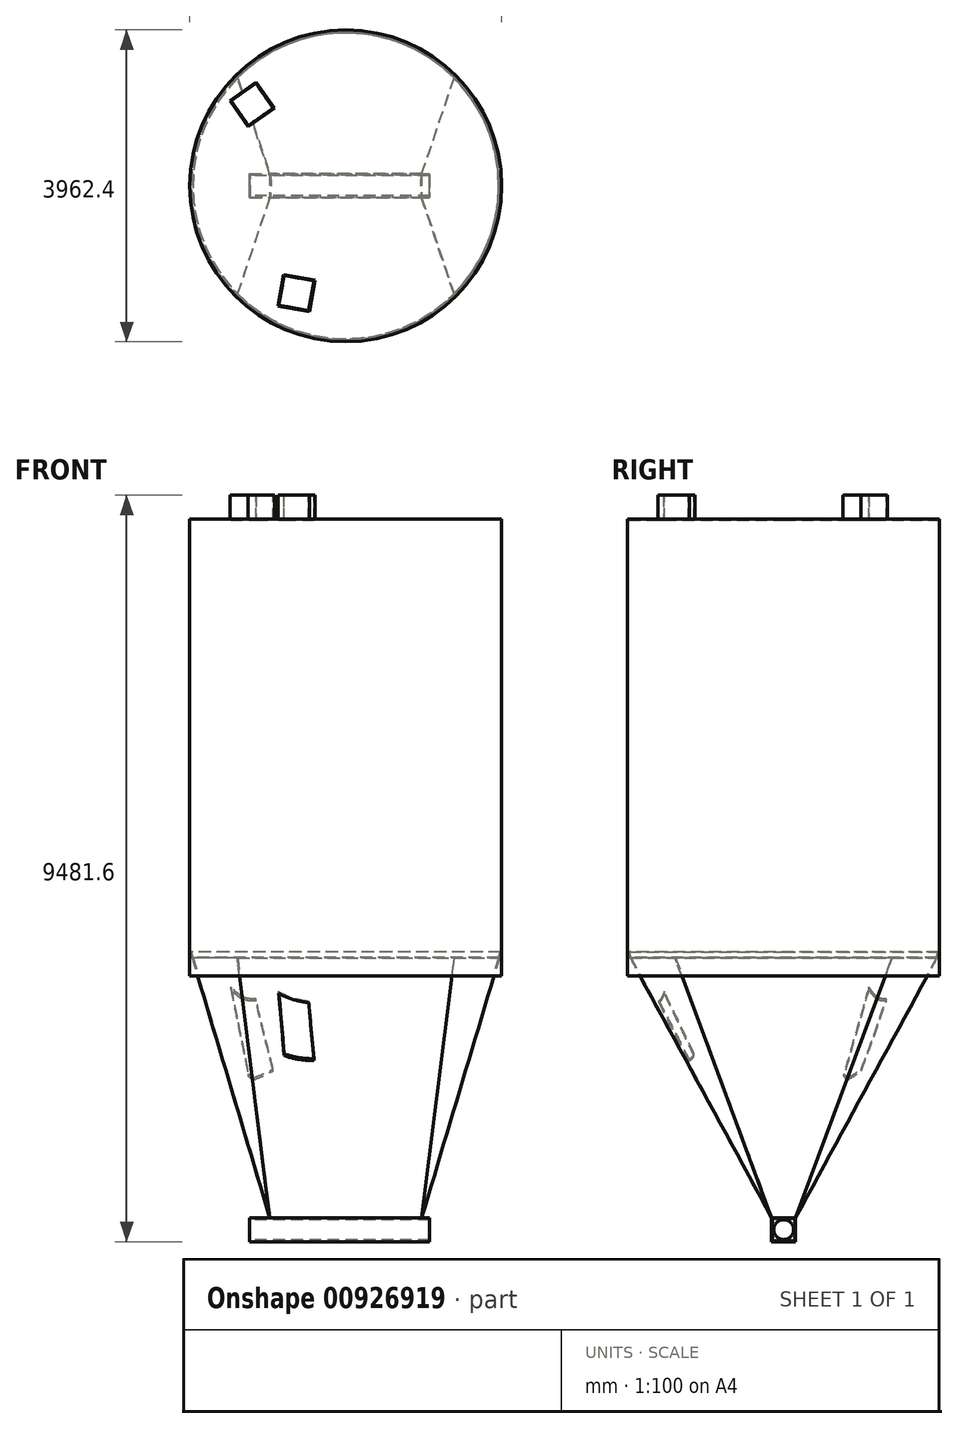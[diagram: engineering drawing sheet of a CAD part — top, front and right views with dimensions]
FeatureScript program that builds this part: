
annotation { "Feature Type Name" : "Feature", "Feature Type Description" : "" }
export const myFeature = defineFeature(function(context is Context, id is Id, definition is map)
    precondition{}
    {
        {
            var Q0;
            Q0=qCreatedBy(makeId("Front.planeOp"),FACE);
            var sketch = newSketch(context, id + "F0", { "sketchPlane" : qUnion([Q0])});
            skLineSegment(sketch, "E0", {"start": v(-1971.2, 73.6) * mm, "end": v(-1961.54, 76.2) * mm});
            skLineSegment(sketch, "E1", {"start": v(-1961.54, 76.2) * mm, "end": v(-1941.82, 2.59) * mm});
            skLineSegment(sketch, "E2", {"start": v(-1941.82, 2.59) * mm, "end": v(-1951.48, 0) * mm});
            skLineSegment(sketch, "E3", {"start": v(-1951.48, 0) * mm, "end": v(-1971.2, 73.6) * mm});
            skLineSegment(sketch, "E4", {"start": v(0, 190.18) * mm, "end": v(0, -283.34) * mm, "construction": true});
            skLineSegment(sketch, "E5.bottom", {"start": v(-1981.2, 5560) * mm, "end": v(-1971.2, 5560) * mm});
            skLineSegment(sketch, "E5.top", {"start": v(-1981.2, -231.2) * mm, "end": v(-1971.2, -231.2) * mm});
            skLineSegment(sketch, "E5.left", {"start": v(-1981.2, 5560) * mm, "end": v(-1981.2, -231.2) * mm});
            skLineSegment(sketch, "E5.right", {"start": v(-1971.2, 5560) * mm, "end": v(-1971.2, -231.2) * mm});
            skSolve(sketch);
        }
        {
            var Q0;
            Q0 = qSketchRegion(id + "F0", true);
            var Q1;
            Q1=sQuery(id+"F0.wireOp",EDGE,"E4");
            revolve(context, id + "F1", {"surfaceOperationType" : NewSurfaceOperationType.NEW, "entities" : qUnion([Q0]), "axis" : qUnion([Q1]), "revolveType" : RevolveType.FULL});
        }
        {
            var Q0;
            Q0=makeQuery(id+"F1.opRevolve","SWEPT_FACE",FACE,{"disambiguationData":[OSD([sQuery(id+"F0.wireOp",EDGE,"E5.bottom")])]});
            var sketch = newSketch(context, id + "F2", { "sketchPlane" : qUnion([Q0])});
            skCircle(sketch, "E6.0", {"center": v(0, 0) * mm, "radius": 1981.2 * mm});
            skSolve(sketch);
        }
        {
            var Q0;
            Q0 = qSketchRegion(id + "F2", true);
            extrude(context, id + "F3", {"entities" : qUnion([Q0]), "operationType" : NewBodyOperationType.ADD, "depth" : 10 * mm, "offsetDistance" : 25.4 * mm});
        }
        {
            var Q0;
            Q0=qCreatedBy(makeId("Top.planeOp"),FACE);
            cPlane(context, id + "F4", {"entities" : qUnion([Q0]), "cplaneType" : CPlaneType.OFFSET, "offset" : 3302 * mm, "oppositeDirection" : true, "width" : 152.4 * mm, "height" : 152.4 * mm});
        }
        {
            var Q0;
            Q0=qCreatedBy(id+"F4.planeOp",FACE);
            var sketch = newSketch(context, id + "F5", { "sketchPlane" : qUnion([Q0])});
            skLineSegment(sketch, "E7.bottom", {"start": v(965.2, 152.4) * mm, "end": v(-965.2, 152.4) * mm});
            skLineSegment(sketch, "E7.top", {"start": v(965.2, -152.4) * mm, "end": v(-965.2, -152.4) * mm});
            skLineSegment(sketch, "E7.left", {"start": v(965.2, 152.4) * mm, "end": v(965.2, -152.4) * mm});
            skLineSegment(sketch, "E7.right", {"start": v(-965.2, 152.4) * mm, "end": v(-965.2, -152.4) * mm});
            skPoint(sketch, "E7.middle", {"position": v(0, 0) * mm});
            skSolve(sketch);
        }
        {
            var Q0;
            Q0=qCreatedBy(makeId("Top.planeOp"),FACE);
            var sketch = newSketch(context, id + "F6", { "sketchPlane" : qUnion([Q0])});
            skCircle(sketch, "E8.0", {"center": v(0, 0) * mm, "radius": 1951.48 * mm});
            skLineSegment(sketch, "E9.bottom", {"start": v(1379.9, 1379.9) * mm, "end": v(-1379.9, 1379.9) * mm, "construction": true});
            skLineSegment(sketch, "E9.top", {"start": v(1379.9, -1379.9) * mm, "end": v(-1379.9, -1379.9) * mm, "construction": true});
            skLineSegment(sketch, "E9.left", {"start": v(1379.9, 1379.9) * mm, "end": v(1379.9, -1379.9) * mm, "construction": true});
            skLineSegment(sketch, "E9.right", {"start": v(-1379.9, 1379.9) * mm, "end": v(-1379.9, -1379.9) * mm, "construction": true});
            skSolve(sketch);
        }
        {
            var Q1;
            Q1 = qSketchRegion(id + "F5", true);
            var Q2;
            Q2 = qSketchRegion(id + "F6", true);
            var Q3;
            Q3=sQuery(id+"F6.wireOp",VERTEX,"E9.bottom.end");
            var Q4;
            Q4=sQuery(id+"F5.wireOp",VERTEX,"E7.bottom.end");
            loft(context, id + "F7", {"sheetProfilesArray" : [{ "sheetProfileEntities" : qUnion([Q1]) }, { "sheetProfileEntities" : qUnion([Q2]) }], "matchConnections" : true, "connections" : [{ "connectionEntities" : qUnion([Q3, Q4]), "connectionEdgeQueries" : qUnion([]), "connectionEdgeParameters" : [] }]});
        }
        {
            var Q0;
            Q0=makeQuery(id+"F7.opLoft","CAP_FACE",FACE,{"disambiguationData":[OSD([makeQuery(id+"F5.imprint","IMPRINT",FACE,{"disambiguationData":[TD([[makeQuery(id+"F5.imprint","IMPRINT",EDGE,{"derivedFrom":sQuery(id+"F5.wireOp",EDGE,"E7.bottom")}),1.0]])]})])],"isStart":true});
            var sketch = newSketch(context, id + "F8", { "sketchPlane" : qUnion([Q0])});
            skLineSegment(sketch, "E10.bottom", {"start": v(-1219.2, 152.4) * mm, "end": v(1219.2, 152.4) * mm});
            skLineSegment(sketch, "E10.top", {"start": v(-1219.2, -152.4) * mm, "end": v(1219.2, -152.4) * mm});
            skLineSegment(sketch, "E10.left", {"start": v(-1219.2, 152.4) * mm, "end": v(-1219.2, -152.4) * mm});
            skLineSegment(sketch, "E10.right", {"start": v(1219.2, 152.4) * mm, "end": v(1219.2, -152.4) * mm});
            skPoint(sketch, "E10.middle", {"position": v(0, 0) * mm});
            skSolve(sketch);
        }
        {
            var Q0;
            Q0 = qSketchRegion(id + "F8", true);
            extrude(context, id + "F9", {"entities" : qUnion([Q0]), "operationType" : NewBodyOperationType.ADD, "depth" : 304.8 * mm, "offsetDistance" : 25.4 * mm});
        }
        {
            var Q0;
            Q0=makeQuery(id+"F7.opLoft","CAP_FACE",FACE,{"disambiguationData":[OSD([makeQuery(id+"F6.imprint","IMPRINT",FACE,{"disambiguationData":[TD([[makeQuery(id+"F6.imprint","IMPRINT",EDGE,{"derivedFrom":sQuery(id+"F6.wireOp",EDGE,"E8.0")}),1.0]])]})])],"isStart":true});
            shell(context, id + "F10", {"entities" : qUnion([Q0]), "thickness" : 10 * mm});
        }
        {
            var Q0;
            Q0=qCreatedBy(makeId("Right.planeOp"),FACE);
            var sketch = newSketch(context, id + "F11", { "sketchPlane" : qUnion([Q0])});
            skCircle(sketch, "E11", {"center": v(0, -3453.68) * mm, "radius": 127 * mm});
            skSolve(sketch);
        }
        {
            var Q0;
            Q0 = qSketchRegion(id + "F11", true);
            extrude(context, id + "F12", {"entities" : qUnion([Q0]), "endBound" : BoundingType.SYMMETRIC, "depth" : 2438.4 * mm, "offsetDistance" : 25.4 * mm});
        }
        {
            var Q0;
            Q0=makeQuery(id+"F9.opExtrude","SWEPT_FACE",FACE,{"disambiguationData":[OSD([sQuery(id+"F8.wireOp",EDGE,"E10.right")])]});
            extrude(context, id + "F13", {"entities" : qUnion([Q0]), "operationType" : NewBodyOperationType.REMOVE, "oppositeDirection" : true, "depth" : 152.4 * mm, "offsetDistance" : 25.4 * mm});
        }
        {
            var Q0;
            Q0=makeQuery(id+"F3.opExtrude","CAP_FACE",FACE,{"disambiguationData":[OSD([sQuery(id+"F2.wireOp",EDGE,"E6.0")])],"isStart":false});
            var sketch = newSketch(context, id + "F14", { "sketchPlane" : qUnion([Q0])});
            skLineSegment(sketch, "E12", {"start": v(-390.61, -1198.02) * mm, "end": v(-463.12, -1597.9) * mm});
            skLineSegment(sketch, "E13", {"start": v(-463.12, -1597.9) * mm, "end": v(-863, -1525.4) * mm});
            skLineSegment(sketch, "E14", {"start": v(-863, -1525.4) * mm, "end": v(-790.5, -1125.52) * mm});
            skLineSegment(sketch, "E15", {"start": v(-790.5, -1125.52) * mm, "end": v(-390.61, -1198.02) * mm});
            skLineSegment(sketch, "E16", {"start": v(-1139.73, 1317.29) * mm, "end": v(-906.72, 984.32) * mm});
            skLineSegment(sketch, "E17", {"start": v(-906.72, 984.32) * mm, "end": v(-1239.7, 751.31) * mm});
            skLineSegment(sketch, "E18", {"start": v(-1239.7, 751.31) * mm, "end": v(-1472.7, 1084.28) * mm});
            skLineSegment(sketch, "E19", {"start": v(-1472.7, 1084.28) * mm, "end": v(-1139.73, 1317.29) * mm});
            skSolve(sketch);
        }
        {
            var Q0;
            Q0 = qSketchRegion(id + "F14", true);
            extrude(context, id + "F15", {"entities" : qUnion([Q0]), "operationType" : NewBodyOperationType.ADD, "depth" : 304.8 * mm, "offsetDistance" : 25.4 * mm});
        }
        {
            var Q0;
            Q0=makeQuery(id+"F15.opExtrude","CAP_FACE",FACE,{"disambiguationData":[OSD([sQuery(id+"F14.wireOp",EDGE,"E16"),sQuery(id+"F14.wireOp",EDGE,"E17"),sQuery(id+"F14.wireOp",EDGE,"E18"),sQuery(id+"F14.wireOp",EDGE,"E19")])],"isStart":false});
            var sketch = newSketch(context, id + "F16", { "sketchPlane" : qUnion([Q0])});
            skLineSegment(sketch, "E20.0", {"start": v(-1142.19, 1303.36) * mm, "end": v(-920.65, 986.78) * mm});
            skLineSegment(sketch, "E20.1", {"start": v(-1458.77, 1081.82) * mm, "end": v(-1142.19, 1303.36) * mm});
            skLineSegment(sketch, "E20.2", {"start": v(-1237.23, 765.24) * mm, "end": v(-1458.77, 1081.82) * mm});
            skLineSegment(sketch, "E20.3", {"start": v(-920.65, 986.78) * mm, "end": v(-1237.23, 765.24) * mm});
            skLineSegment(sketch, "E21.0", {"start": v(-782.44, -1137.14) * mm, "end": v(-402.23, -1206.08) * mm});
            skLineSegment(sketch, "E21.1", {"start": v(-851.37, -1517.34) * mm, "end": v(-782.44, -1137.14) * mm});
            skLineSegment(sketch, "E21.2", {"start": v(-471.17, -1586.28) * mm, "end": v(-851.37, -1517.34) * mm});
            skLineSegment(sketch, "E21.3", {"start": v(-402.23, -1206.08) * mm, "end": v(-471.17, -1586.28) * mm});
            skSolve(sketch);
        }
        {
            var Q0;
            Q0 = qSketchRegion(id + "F16", true);
            extrude(context, id + "F17", {"entities" : qUnion([Q0]), "operationType" : NewBodyOperationType.REMOVE, "endBound" : BoundingType.THROUGH_ALL, "oppositeDirection" : true, "depth" : 25.4 * mm, "offsetDistance" : 25.4 * mm});
        }
    });
